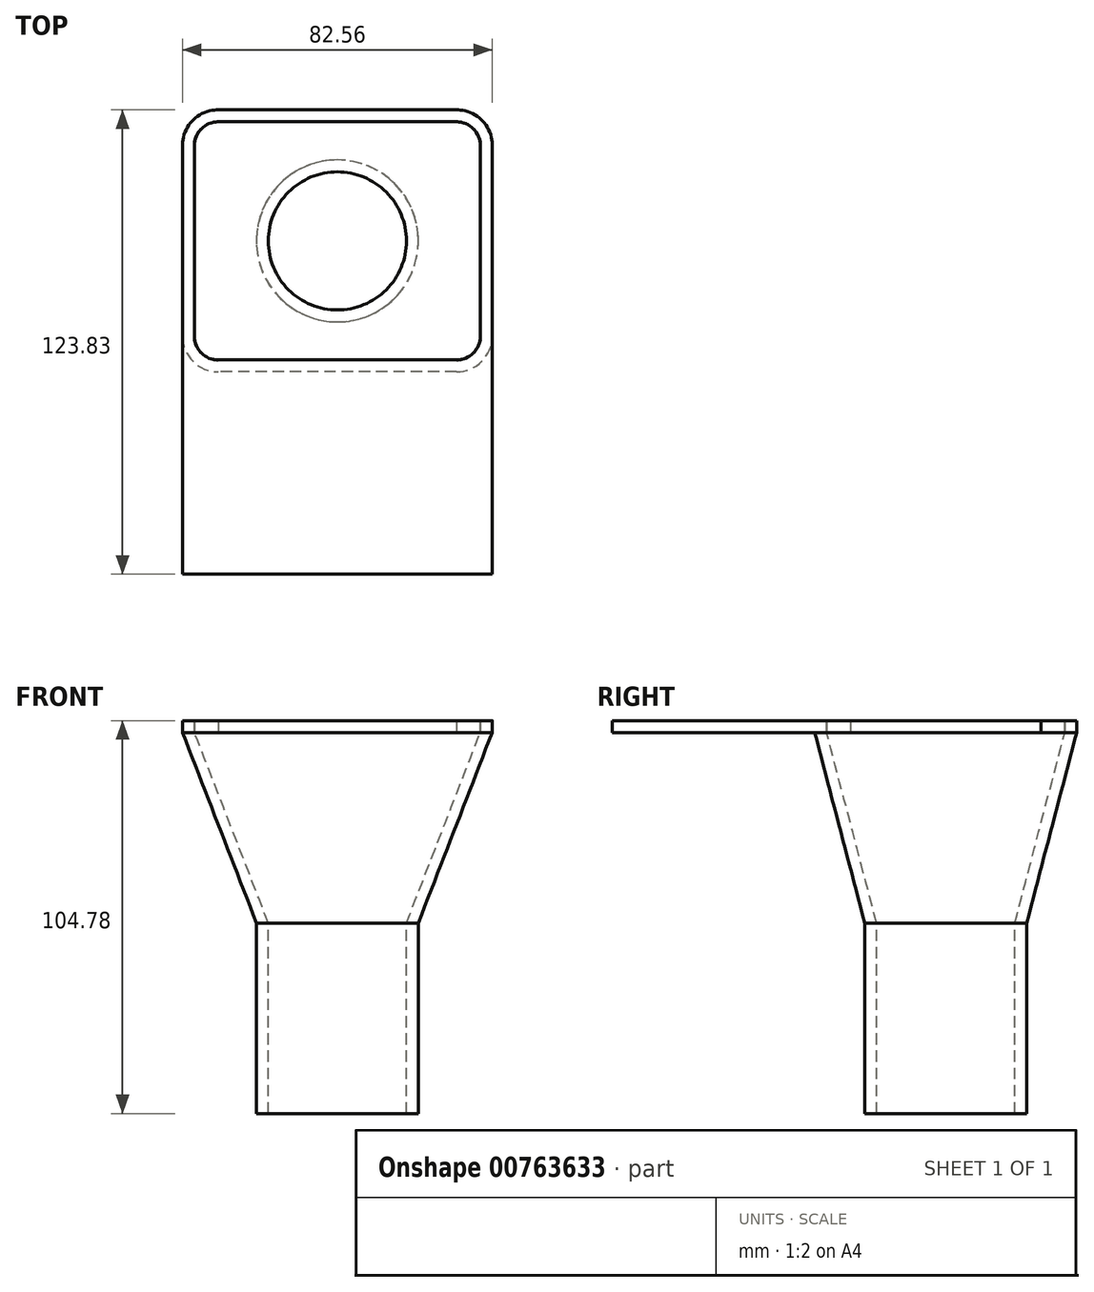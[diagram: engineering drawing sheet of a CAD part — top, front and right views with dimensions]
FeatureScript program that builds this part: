
annotation { "Feature Type Name" : "Feature", "Feature Type Description" : "" }
export const myFeature = defineFeature(function(context is Context, id is Id, definition is map)
    precondition{}
    {
        {
            var Q0;
            Q0=qCreatedBy(makeId("Top.planeOp"),FACE);
            cPlane(context, id + "F0", {"entities" : qUnion([Q0]), "cplaneType" : CPlaneType.OFFSET, "offset" : 50.8 * mm, "width" : 152.4 * mm, "height" : 152.4 * mm});
        }
        {
            var Q0;
            Q0=qCreatedBy(makeId("Top.planeOp"),FACE);
            var sketch = newSketch(context, id + "F1", { "sketchPlane" : qUnion([Q0])});
            skCircle(sketch, "E0", {"center": v(0, 0) * mm, "radius": 18.41 * mm});
            skSolve(sketch);
        }
        {
            var Q0;
            Q0=qCreatedBy(id+"F0.planeOp",FACE);
            var sketch = newSketch(context, id + "F2", { "sketchPlane" : qUnion([Q0])});
            skLineSegment(sketch, "E1.bottom", {"start": v(31.75, -31.75) * mm, "end": v(-31.75, -31.75) * mm, "construction": true});
            skLineSegment(sketch, "E1.top", {"start": v(31.75, 31.75) * mm, "end": v(-31.75, 31.75) * mm, "construction": true});
            skLineSegment(sketch, "E1.left", {"start": v(38.1, -25.4) * mm, "end": v(38.1, 25.4) * mm, "construction": true});
            skLineSegment(sketch, "E1.right", {"start": v(-38.1, -25.4) * mm, "end": v(-38.1, 25.4) * mm, "construction": true});
            skPoint(sketch, "E1.middle", {"position": v(0, 0) * mm});
            skPoint(sketch, "E2.visualSharp", {"position": v(-38.1, 31.75) * mm});
            skArc(sketch, "E2.filletArc", {"start": v(-31.75, 31.75) * mm, "mid": v(-36.24, 29.9) * mm, "end": v(-38.1, 25.4) * mm, "construction": true});
            skPoint(sketch, "E3.visualSharp", {"position": v(38.1, 31.75) * mm});
            skArc(sketch, "E3.filletArc", {"start": v(38.1, 25.4) * mm, "mid": v(36.24, 29.9) * mm, "end": v(31.75, 31.75) * mm, "construction": true});
            skPoint(sketch, "E4.visualSharp", {"position": v(38.1, -31.75) * mm});
            skArc(sketch, "E4.filletArc", {"start": v(31.75, -31.75) * mm, "mid": v(36.24, -29.9) * mm, "end": v(38.1, -25.4) * mm, "construction": true});
            skPoint(sketch, "E5.visualSharp", {"position": v(-38.1, -31.75) * mm});
            skArc(sketch, "E5.filletArc", {"start": v(-38.1, -25.4) * mm, "mid": v(-36.24, -29.9) * mm, "end": v(-31.75, -31.75) * mm, "construction": true});
            skLineSegment(sketch, "E6.0", {"start": v(31.75, 34.93) * mm, "end": v(-31.75, 34.92) * mm});
            skArc(sketch, "E6.1", {"start": v(41.27, 25.4) * mm, "mid": v(38.49, 32.14) * mm, "end": v(31.75, 34.92) * mm});
            skArc(sketch, "E6.2", {"start": v(-31.75, 34.92) * mm, "mid": v(-38.49, 32.14) * mm, "end": v(-41.27, 25.4) * mm});
            skLineSegment(sketch, "E6.3", {"start": v(41.27, -25.4) * mm, "end": v(41.27, 25.4) * mm});
            skLineSegment(sketch, "E6.4", {"start": v(-41.27, -25.4) * mm, "end": v(-41.28, 25.4) * mm});
            skArc(sketch, "E6.5", {"start": v(-41.27, -25.4) * mm, "mid": v(-38.49, -32.14) * mm, "end": v(-31.75, -34.92) * mm});
            skLineSegment(sketch, "E6.6", {"start": v(31.75, -34.92) * mm, "end": v(-31.75, -34.92) * mm});
            skArc(sketch, "E6.7", {"start": v(31.75, -34.92) * mm, "mid": v(38.49, -32.14) * mm, "end": v(41.28, -25.4) * mm});
            skSolve(sketch);
        }
        {
            var Q0;
            Q0=qCreatedBy(makeId("Top.planeOp"),FACE);
            var sketch = newSketch(context, id + "F3", { "sketchPlane" : qUnion([Q0])});
            skCircle(sketch, "E7", {"center": v(0, 0) * mm, "radius": 18.41 * mm, "construction": true});
            skCircle(sketch, "E8.0", {"center": v(0, 0) * mm, "radius": 21.59 * mm});
            skSolve(sketch);
        }
        {
            var Q0;
            Q0=qCreatedBy(makeId("Top.planeOp"),FACE);
            var sketch = newSketch(context, id + "F4", { "sketchPlane" : qUnion([Q0])});
            skCircle(sketch, "E9.0", {"center": v(0, 0) * mm, "radius": 18.41 * mm});
            skCircle(sketch, "E9.1", {"center": v(0, 0) * mm, "radius": 21.59 * mm});
            skSolve(sketch);
        }
        {
            var Q0;
            Q0=qCreatedBy(makeId("Top.planeOp"),FACE);
            var sketch = newSketch(context, id + "F5", { "sketchPlane" : qUnion([Q0])});
            skCircle(sketch, "E10.0", {"center": v(0, 0) * mm, "radius": 18.41 * mm});
            skCircle(sketch, "E10.1", {"center": v(0, 0) * mm, "radius": 21.59 * mm, "construction": true});
            skSolve(sketch);
        }
        {
            var Q0;
            Q0=qCreatedBy(id+"F0.planeOp",FACE);
            var sketch = newSketch(context, id + "F6", { "sketchPlane" : qUnion([Q0])});
            skLineSegment(sketch, "E11.0", {"start": v(31.75, -31.75) * mm, "end": v(-31.75, -31.75) * mm});
            skLineSegment(sketch, "E11.1", {"start": v(31.75, 31.75) * mm, "end": v(-31.75, 31.75) * mm});
            skLineSegment(sketch, "E11.2", {"start": v(38.1, -25.4) * mm, "end": v(38.1, 25.4) * mm});
            skLineSegment(sketch, "E11.3", {"start": v(-38.1, -25.4) * mm, "end": v(-38.1, 25.4) * mm});
            skPoint(sketch, "E11.4", {"position": v(0, 0) * mm});
            skPoint(sketch, "E11.5", {"position": v(-38.1, 31.75) * mm});
            skArc(sketch, "E11.6", {"start": v(-31.75, 31.75) * mm, "mid": v(-36.24, 29.9) * mm, "end": v(-38.1, 25.4) * mm});
            skPoint(sketch, "E11.7", {"position": v(38.1, 31.75) * mm});
            skArc(sketch, "E11.8", {"start": v(38.1, 25.4) * mm, "mid": v(36.24, 29.9) * mm, "end": v(31.75, 31.75) * mm});
            skPoint(sketch, "E11.9", {"position": v(38.1, -31.75) * mm});
            skArc(sketch, "E11.10", {"start": v(31.75, -31.75) * mm, "mid": v(36.24, -29.9) * mm, "end": v(38.1, -25.4) * mm});
            skPoint(sketch, "E11.11", {"position": v(-38.1, -31.75) * mm});
            skArc(sketch, "E11.12", {"start": v(-38.1, -25.4) * mm, "mid": v(-36.24, -29.9) * mm, "end": v(-31.75, -31.75) * mm});
            skLineSegment(sketch, "E11.13", {"start": v(31.75, 34.93) * mm, "end": v(-31.75, 34.92) * mm, "construction": true});
            skArc(sketch, "E11.14", {"start": v(41.27, 25.4) * mm, "mid": v(38.49, 32.14) * mm, "end": v(31.75, 34.92) * mm, "construction": true});
            skArc(sketch, "E11.15", {"start": v(-31.75, 34.92) * mm, "mid": v(-38.49, 32.14) * mm, "end": v(-41.27, 25.4) * mm, "construction": true});
            skLineSegment(sketch, "E11.16", {"start": v(41.27, -25.4) * mm, "end": v(41.27, 25.4) * mm, "construction": true});
            skLineSegment(sketch, "E11.17", {"start": v(-41.27, -25.4) * mm, "end": v(-41.28, 25.4) * mm, "construction": true});
            skArc(sketch, "E11.18", {"start": v(-41.27, -25.4) * mm, "mid": v(-38.49, -32.14) * mm, "end": v(-31.75, -34.92) * mm, "construction": true});
            skLineSegment(sketch, "E11.19", {"start": v(31.75, -34.92) * mm, "end": v(-31.75, -34.92) * mm, "construction": true});
            skArc(sketch, "E11.20", {"start": v(31.75, -34.92) * mm, "mid": v(38.49, -32.14) * mm, "end": v(41.28, -25.4) * mm, "construction": true});
            skSolve(sketch);
        }
        {
            var Q0;
            Q0 = qSketchRegion(id + "F2", true);
            var Q1;
            Q1 = qSketchRegion(id + "F3", true);
            loft(context, id + "F7", {"sheetProfilesArray" : [{ "sheetProfileEntities" : qUnion([Q0]) }, { "sheetProfileEntities" : qUnion([Q1]) }]});
        }
        {
            var Q1;
            Q1 = qSketchRegion(id + "F5", true);
            var Q2;
            Q2 = qSketchRegion(id + "F6", true);
            loft(context, id + "F8", {"operationType" : NewBodyOperationType.REMOVE, "sheetProfilesArray" : [{ "sheetProfileEntities" : qUnion([Q1]) }, { "sheetProfileEntities" : qUnion([Q2]) }]});
        }
        {
            var Q0;
            Q0 = qSketchRegion(id + "F4", true);
            extrude(context, id + "F9", {"entities" : qUnion([Q0]), "operationType" : NewBodyOperationType.ADD, "oppositeDirection" : true, "depth" : 50.8 * mm, "offsetDistance" : 25.4 * mm});
        }
        {
            var Q0;
            Q0=qCreatedBy(id+"F0.planeOp",FACE);
            var sketch = newSketch(context, id + "F10", { "sketchPlane" : qUnion([Q0])});
            skFitSpline(sketch, "E12.0", {"points": [v(-41.28, 25.4) * mm, v(-41.28, 26.22) * mm, v(-41.07, 27.7) * mm, v(-40.42, 29.48) * mm, v(-39.58, 30.9) * mm, v(-38.6, 32.08) * mm, v(-37.42, 33.1) * mm, v(-35.98, 34) * mm, v(-34.16, 34.7) * mm, v(-32.6, 34.92) * mm, v(-31.75, 34.92) * mm]});
            skFitSpline(sketch, "E13.0", {"points": [v(-31.75, 34.92) * mm, v(-10.58, 34.92) * mm, v(10.58, 34.92) * mm, v(31.75, 34.92) * mm]});
            skFitSpline(sketch, "E14.0", {"points": [v(31.75, 34.92) * mm, v(32.6, 34.92) * mm, v(34.16, 34.7) * mm, v(35.98, 34) * mm, v(37.42, 33.1) * mm, v(38.6, 32.08) * mm, v(39.58, 30.9) * mm, v(40.42, 29.48) * mm, v(41.07, 27.7) * mm, v(41.27, 26.22) * mm, v(41.27, 25.4) * mm]});
            skLineSegment(sketch, "E15", {"start": v(41.27, 25.4) * mm, "end": v(41.27, -88.9) * mm});
            skLineSegment(sketch, "E16", {"start": v(-41.28, 25.4) * mm, "end": v(-41.28, -88.9) * mm});
            skLineSegment(sketch, "E17", {"start": v(-41.27, -88.9) * mm, "end": v(41.27, -88.9) * mm});
            skFitSpline(sketch, "E18.0", {"points": [v(31.75, 31.75) * mm, v(10.58, 31.75) * mm, v(-10.58, 31.75) * mm, v(-31.75, 31.75) * mm]});
            skFitSpline(sketch, "E19.0", {"points": [v(38.1, 25.4) * mm, v(38.1, 25.95) * mm, v(37.96, 26.94) * mm, v(37.53, 28.12) * mm, v(36.97, 29.07) * mm, v(36.3, 29.86) * mm, v(35.53, 30.54) * mm, v(34.57, 31.13) * mm, v(33.35, 31.6) * mm, v(32.32, 31.75) * mm, v(31.75, 31.75) * mm]});
            skFitSpline(sketch, "E20.0", {"points": [v(38.1, -25.4) * mm, v(38.1, -8.47) * mm, v(38.1, 8.47) * mm, v(38.1, 25.4) * mm]});
            skPoint(sketch, "E21.0", {"position": v(36.24, -29.9) * mm});
            skFitSpline(sketch, "E22.0", {"points": [v(31.75, -31.75) * mm, v(32.32, -31.75) * mm, v(33.35, -31.6) * mm, v(34.57, -31.13) * mm, v(35.53, -30.54) * mm, v(36.3, -29.86) * mm, v(36.97, -29.07) * mm, v(37.53, -28.12) * mm, v(37.96, -26.94) * mm, v(38.1, -25.95) * mm, v(38.1, -25.4) * mm]});
            skFitSpline(sketch, "E23.0", {"points": [v(-31.75, -31.75) * mm, v(-10.58, -31.75) * mm, v(10.58, -31.75) * mm, v(31.75, -31.75) * mm]});
            skFitSpline(sketch, "E24.0", {"points": [v(-38.1, -25.4) * mm, v(-38.1, -25.95) * mm, v(-37.96, -26.94) * mm, v(-37.53, -28.12) * mm, v(-36.97, -29.07) * mm, v(-36.3, -29.86) * mm, v(-35.53, -30.54) * mm, v(-34.57, -31.13) * mm, v(-33.35, -31.6) * mm, v(-32.32, -31.75) * mm, v(-31.75, -31.75) * mm]});
            skFitSpline(sketch, "E25.0", {"points": [v(-38.1, 25.4) * mm, v(-38.1, 8.47) * mm, v(-38.1, -8.47) * mm, v(-38.1, -25.4) * mm]});
            skFitSpline(sketch, "E26.0", {"points": [v(-31.75, 31.75) * mm, v(-32.32, 31.75) * mm, v(-33.35, 31.6) * mm, v(-34.57, 31.13) * mm, v(-35.53, 30.54) * mm, v(-36.3, 29.86) * mm, v(-36.97, 29.07) * mm, v(-37.53, 28.12) * mm, v(-37.96, 26.94) * mm, v(-38.1, 25.95) * mm, v(-38.1, 25.4) * mm]});
            skSolve(sketch);
        }
        {
            var Q0;
            Q0 = qSketchRegion(id + "F10", true);
            extrude(context, id + "F11", {"entities" : qUnion([Q0]), "operationType" : NewBodyOperationType.ADD, "depth" : 3.17 * mm, "offsetDistance" : 25.4 * mm});
        }
    });
